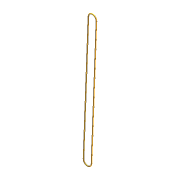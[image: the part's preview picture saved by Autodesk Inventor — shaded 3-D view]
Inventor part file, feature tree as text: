
AUTODESK INVENTOR PART (.ipt)
format: ipt  version: 2012 (Build 160160000, 160)  size: 85,504 bytes
history: native  units: in
note: dims shown in document units (in); Inventor stores cm internally (conversion verified against a paired STEP export)
features: extrude x1, fillet x1, sketch x1
ambient origin geometry x8: Origin, YZ Plane, XZ Plane, XY Plane, X Axis, Y Axis, Z Axis, Center Point
bodies: Solid1 (feature_tree)
feature tree (3):
  extrude  "Extrusion1"  Depth=0.1875in TaperAngle=0.0deg
  fillet  "Fillet1"  Radius=0.0938in
  sketch  "Sketch1"  dims[d0=0.1875in d1=0.1875in d2=0.0in d3=0.0938in]
